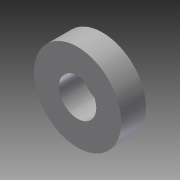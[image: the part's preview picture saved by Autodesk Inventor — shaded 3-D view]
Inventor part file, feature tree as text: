
AUTODESK INVENTOR PART (.ipt)
format: ipt  version: 2013 (Build 170138000, 138)  size: 78,848 bytes
history: native  units: in
note: dims shown in document units (in); Inventor stores cm internally (conversion verified against a paired STEP export)
features: extrude x1, sketch x1
ambient origin geometry x8: Origin, YZ Plane, XZ Plane, XY Plane, X Axis, Y Axis, Z Axis, Center Point
bodies: Solid1 (feature_tree)
feature tree (2):
  extrude  "Extrusion1"  Depth=0.4724in
  sketch  "Sketch1"  dims[d0=1.1024in d2=0.4724in d3=0.315in d4=0.0in]
